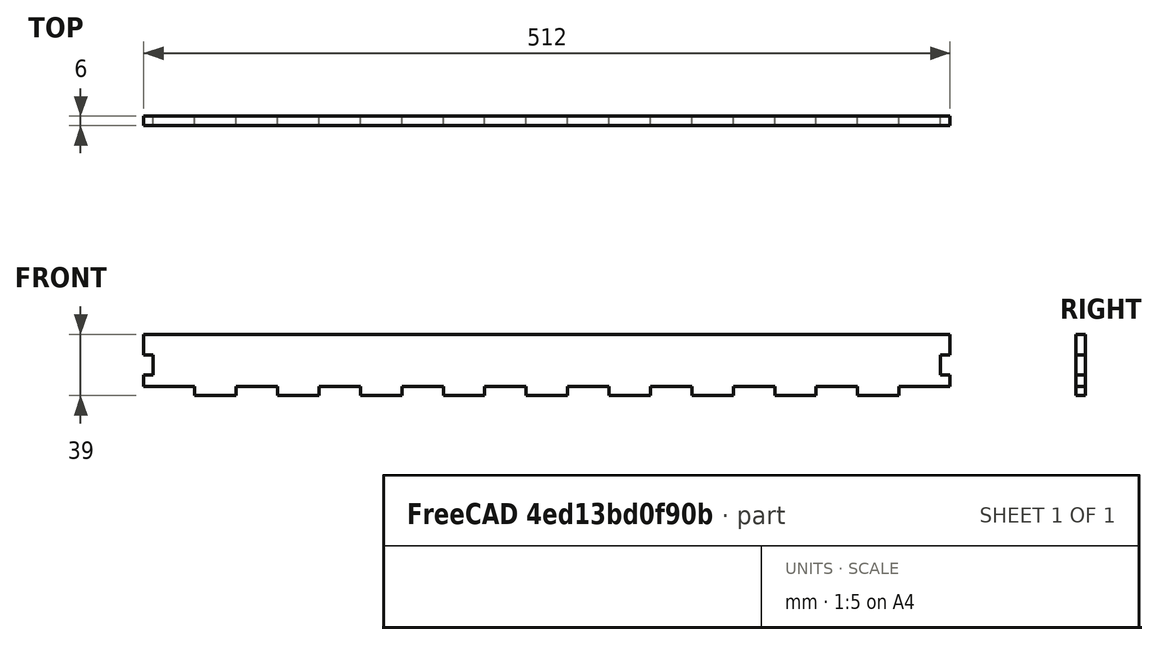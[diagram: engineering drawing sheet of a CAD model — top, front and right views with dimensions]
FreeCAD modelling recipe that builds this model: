
FCSTD DOCUMENT  (FreeCAD 0.16R6527 (Git))
Label: side_500
License: All rights reserved
LicenseURL: http://en.wikipedia.org/wiki/All_rights_reserved
objects: Part::Box×4, Part::FeaturePython×3, Part::Cut×3
note: 10 computed .brp shape members not serialized (recipe doc carries the construction recipe); baked Part::Feature solids carry a one-line shape summary decoded from their .brp

FEATURE [Part::Box] Box  label="Strip"
  Height = 39
  Length = 512
  Width = 6
  expr: Height = bottom#Slab.Height + strip_500#Strip.Height + glass#Glass.Height - 1mm
  expr: Width = bottom#Slab.Height
  expr: Length = bottom#Slab.Length
FEATURE [Part::Box] Box001  label="Horizontal_hole"
  Height = 6
  Length = 26.3158
  Width = 10
  expr: Height = bottom#Slab.Height
  expr: Length = bottom#Horizontal_hole.Length
FEATURE [Part::FeaturePython] Array  label="Horizontal_Array"  # Draft array (typed FeaturePython)
  Angle = 360
  ArrayType = 0
  Axis = (0,0,1)
  Base = -> Box001
  Center = (0,0,0)
  Fuse = false
  IntervalAxis = (0,0,0)
  IntervalX = (52.6316,0,0)
  IntervalY = (0,1,0)
  IntervalZ = (0,0,0)
  NumberPolar = 1
  NumberX = 10
  NumberY = 0
  NumberZ = 0
  Placement = pos=(6,0,0) rot=(0,0,1;0rad)
  expr: Placement.Base.x = bottom#Slab.Height
  expr: IntervalX.x = bottom#Horizontal_hole.Length * 2
FEATURE [Part::Cut] Cut  label="Horizontal_Cut"
  Base = -> Box
  Tool = -> Array
FEATURE [Part::Box] Box002  label="Vertical_Hole"
  Height = 13
  Length = 6
  Placement = pos=(0,0,13) rot=(0,0,1;0rad)
  Width = 10
  expr: Placement.Base.z = Vertical_Hole.Height
  expr: Height = Strip.Height / 3
  expr: Length = Strip.Width
FEATURE [Part::FeaturePython] Array002  label="Vertical_Array"  # Draft array (typed FeaturePython)
  Angle = 360
  ArrayType = 0
  Axis = (0,0,1)
  Base = -> Box002
  Center = (0,0,0)
  Fuse = false
  IntervalAxis = (0,0,0)
  IntervalX = (506,0,0)
  IntervalY = (0,1,0)
  IntervalZ = (0,0,0)
  NumberPolar = 1
  NumberX = 2
  NumberY = 1
  NumberZ = 1
  expr: IntervalX.x = Strip.Length - Strip.Width
FEATURE [Part::Cut] Cut001  label="Cut"
  Base = -> Cut
  Tool = -> Array002
FEATURE [Part::Box] Box003  label="Hook_hole"
  Height = 6
  Length = 6
  Width = 10
  expr: Height = Strip.Width
  expr: Length = Strip.Width
FEATURE [Part::FeaturePython] Array004  label="Hook_Array"  # Draft array (typed FeaturePython)
  Angle = 360
  ArrayType = 0
  Axis = (0,0,1)
  Base = -> Box003
  Center = (0,0,0)
  Fuse = false
  IntervalAxis = (0,0,0)
  IntervalX = (506,0,0)
  IntervalY = (0,1,0)
  IntervalZ = (0,0,0)
  NumberPolar = 1
  NumberX = 2
  NumberY = 1
  NumberZ = 1
  expr: IntervalX.x = Strip.Length - Strip.Width
FEATURE [Part::Cut] Cut002  label="Hook_Cut"
  Base = -> Cut001
  Tool = -> Array004
